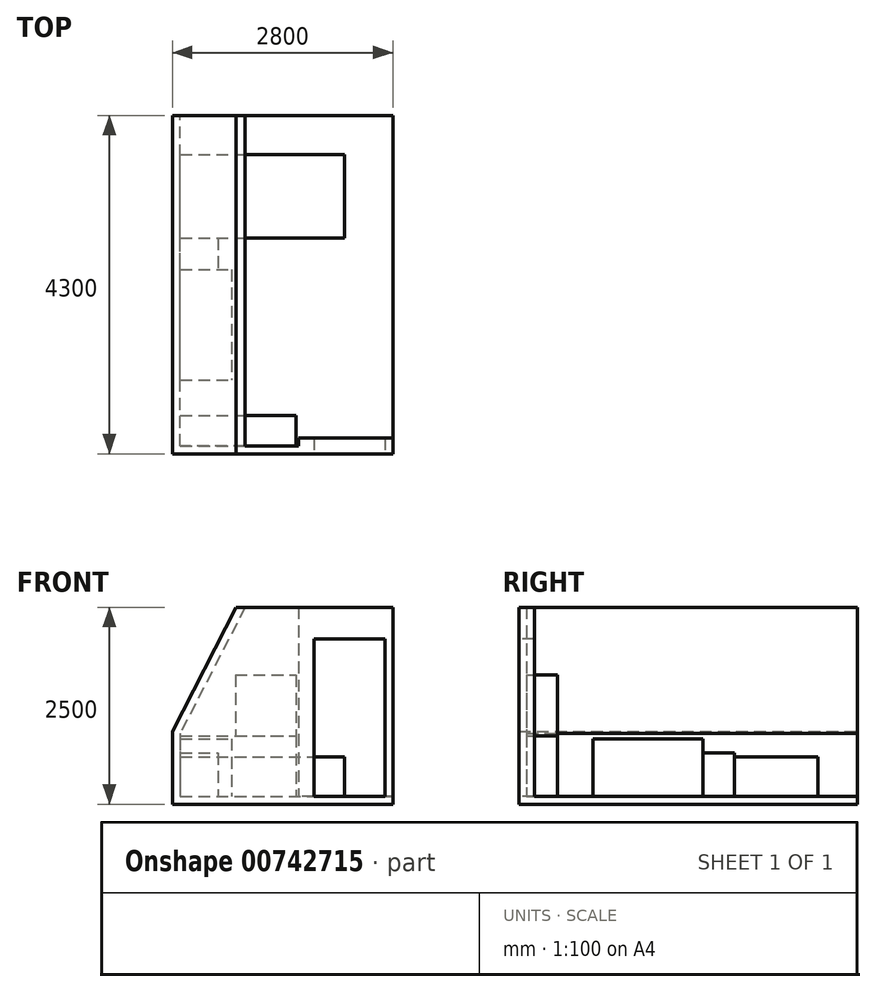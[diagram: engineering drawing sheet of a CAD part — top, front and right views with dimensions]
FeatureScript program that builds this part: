
annotation { "Feature Type Name" : "Feature", "Feature Type Description" : "" }
export const myFeature = defineFeature(function(context is Context, id is Id, definition is map)
    precondition{}
    {
        {
            var Q0;
            Q0=qCreatedBy(makeId("Front.planeOp"),FACE);
            var sketch = newSketch(context, id + "F0", { "sketchPlane" : qUnion([Q0])});
            skLineSegment(sketch, "E0", {"start": v(-1350, 800) * mm, "end": v(-1350, 0) * mm});
            skLineSegment(sketch, "E1", {"start": v(-1350, 0) * mm, "end": v(1350, 0) * mm});
            skLineSegment(sketch, "E2", {"start": v(1350, 0) * mm, "end": v(1350, 2400) * mm});
            skLineSegment(sketch, "E3", {"start": v(1350, 2400) * mm, "end": v(-525.38, 2400) * mm});
            skLineSegment(sketch, "E4", {"start": v(-525.38, 2400) * mm, "end": v(-1350, 800) * mm});
            skSolve(sketch);
        }
        {
            var Q0;
            Q0=makeQuery(id+"F0.imprint","IMPRINT",FACE,{"disambiguationData":[TD([[makeQuery(id+"F0.imprint","IMPRINT",EDGE,{"derivedFrom":sQuery(id+"F0.wireOp",EDGE,"E0")}),1.0]])]});
            extrude(context, id + "F1", {"entities" : qUnion([Q0]), "endBound" : BoundingType.SYMMETRIC, "depth" : 4200 * mm, "offsetDistance" : 25 * mm});
        }
        {
            var Q0;
            Q0=makeQuery(id+"F1.opExtrude","CAP_FACE",FACE,{"disambiguationData":[OSD([sQuery(id+"F0.wireOp",EDGE,"E0"),sQuery(id+"F0.wireOp",EDGE,"E1"),sQuery(id+"F0.wireOp",EDGE,"E2"),sQuery(id+"F0.wireOp",EDGE,"E3"),sQuery(id+"F0.wireOp",EDGE,"E4")])],"isStart":true});
            var Q1;
            Q1=makeQuery(id+"F1.opExtrude","SWEPT_FACE",FACE,{"disambiguationData":[OSD([sQuery(id+"F0.wireOp",EDGE,"E3")])]});
            var Q2;
            Q2=makeQuery(id+"F1.opExtrude","SWEPT_FACE",FACE,{"disambiguationData":[OSD([sQuery(id+"F0.wireOp",EDGE,"E2")])]});
            shell(context, id + "F2", {"entities" : qUnion([Q0, Q1, Q2]), "thickness" : 100 * mm, "oppositeDirection" : true});
        }
        {
            var Q0;
            Q0=makeQuery(id+"F2.opShell","OFFSET_FACE",FACE,{"disambiguationData":[OSD([sQuery(id+"F0.wireOp",EDGE,"E1")])]});
            var sketch = newSketch(context, id + "F3", { "sketchPlane" : qUnion([Q0])});
            skLineSegment(sketch, "E5.bottom", {"start": v(-1350, 1600) * mm, "end": v(740, 1600) * mm});
            skLineSegment(sketch, "E5.top", {"start": v(-1350, 540) * mm, "end": v(740, 540) * mm});
            skLineSegment(sketch, "E5.left", {"start": v(-1350, 1600) * mm, "end": v(-1350, 540) * mm});
            skLineSegment(sketch, "E5.right", {"start": v(740, 1600) * mm, "end": v(740, 540) * mm});
            skSolve(sketch);
        }
        {
            var Q0;
            Q0 = qSketchRegion(id + "F3", true);
            extrude(context, id + "F4", {"entities" : qUnion([Q0]), "depth" : 500 * mm, "offsetDistance" : 25 * mm});
        }
        {
            var Q0;
            Q0=makeQuery(id+"F2.opShell","OFFSET_FACE",FACE,{"disambiguationData":[OSD([sQuery(id+"F0.wireOp",EDGE,"E1")])]});
            var sketch = newSketch(context, id + "F5", { "sketchPlane" : qUnion([Q0])});
            skLineSegment(sketch, "E6.bottom", {"start": v(1350, -2100) * mm, "end": v(150, -2100) * mm});
            skLineSegment(sketch, "E6.top", {"start": v(1350, -2000) * mm, "end": v(150, -2000) * mm});
            skLineSegment(sketch, "E6.left", {"start": v(1350, -2100) * mm, "end": v(1350, -2000) * mm});
            skLineSegment(sketch, "E6.right", {"start": v(150, -2100) * mm, "end": v(150, -2000) * mm});
            skSolve(sketch);
        }
        {
            var Q0;
            Q0 = qSketchRegion(id + "F5", true);
            var Q1;
            Q1=makeQuery(id+"F1.opExtrude","SWEPT_FACE",FACE,{"disambiguationData":[OSD([sQuery(id+"F0.wireOp",EDGE,"E3")])]});
            extrude(context, id + "F6", {"entities" : qUnion([Q0]), "operationType" : NewBodyOperationType.ADD, "endBound" : BoundingType.UP_TO_SURFACE, "depth" : 25 * mm, "endBoundEntityFace" : qUnion([Q1]), "offsetDistance" : 25 * mm});
        }
        {
            var Q0;
            Q0=makeQuery(id+"F1.opExtrude","CAP_FACE",FACE,{"disambiguationData":[OSD([sQuery(id+"F0.wireOp",EDGE,"E0"),sQuery(id+"F0.wireOp",EDGE,"E1"),sQuery(id+"F0.wireOp",EDGE,"E2"),sQuery(id+"F0.wireOp",EDGE,"E3"),sQuery(id+"F0.wireOp",EDGE,"E4")])],"isStart":false});
            var sketch = newSketch(context, id + "F7", { "sketchPlane" : qUnion([Q0])});
            skLineSegment(sketch, "E7.bottom", {"start": v(1250, 0) * mm, "end": v(350, 0) * mm});
            skLineSegment(sketch, "E7.top", {"start": v(1250, 2000) * mm, "end": v(350, 2000) * mm});
            skLineSegment(sketch, "E7.left", {"start": v(1250, 0) * mm, "end": v(1250, 2000) * mm});
            skLineSegment(sketch, "E7.right", {"start": v(350, 0) * mm, "end": v(350, 2000) * mm});
            skSolve(sketch);
        }
        {
            var Q0;
            Q0 = qSketchRegion(id + "F7", true);
            extrude(context, id + "F8", {"entities" : qUnion([Q0]), "operationType" : NewBodyOperationType.REMOVE, "oppositeDirection" : true, "depth" : 1000 * mm, "offsetDistance" : 25 * mm});
        }
        {
            var Q0;
            Q0=makeQuery(id+"F8.boolean.opBoolean","MERGE",FACE,{"derivedFrom":[makeQuery(id+"F2.opShell","OFFSET_FACE",FACE,{"disambiguationData":[OSD([sQuery(id+"F0.wireOp",EDGE,"E1")])]}),makeQuery(id+"F8.opExtrude","SWEPT_FACE",FACE,{"disambiguationData":[OSD([sQuery(id+"F7.wireOp",EDGE,"E7.bottom")])]})]});
            var sketch = newSketch(context, id + "F9", { "sketchPlane" : qUnion([Q0])});
            skLineSegment(sketch, "E8.bottom", {"start": v(-1350, -2100) * mm, "end": v(120, -2100) * mm});
            skLineSegment(sketch, "E8.top", {"start": v(-1350, -1710) * mm, "end": v(120, -1710) * mm});
            skLineSegment(sketch, "E8.left", {"start": v(-1350, -2100) * mm, "end": v(-1350, -1710) * mm});
            skLineSegment(sketch, "E8.right", {"start": v(120, -2100) * mm, "end": v(120, -1710) * mm});
            skSolve(sketch);
        }
        {
            var Q0;
            Q0 = qSketchRegion(id + "F9", true);
            extrude(context, id + "F10", {"entities" : qUnion([Q0]), "depth" : 770 * mm, "offsetDistance" : 25 * mm});
        }
        {
            var Q0;
            Q0=makeQuery(id+"F10.opExtrude","CAP_FACE",FACE,{"disambiguationData":[OSD([sQuery(id+"F9.wireOp",EDGE,"E8.bottom"),sQuery(id+"F9.wireOp",EDGE,"E8.top"),sQuery(id+"F9.wireOp",EDGE,"E8.left"),sQuery(id+"F9.wireOp",EDGE,"E8.right")])],"isStart":false});
            var sketch = newSketch(context, id + "F11", { "sketchPlane" : qUnion([Q0])});
            skLineSegment(sketch, "E9.bottom", {"start": v(120, -2100) * mm, "end": v(-650, -2100) * mm});
            skLineSegment(sketch, "E9.top", {"start": v(120, -1710) * mm, "end": v(-650, -1710) * mm});
            skLineSegment(sketch, "E9.left", {"start": v(120, -2100) * mm, "end": v(120, -1710) * mm});
            skLineSegment(sketch, "E9.right", {"start": v(-650, -2100) * mm, "end": v(-650, -1710) * mm});
            skSolve(sketch);
        }
        {
            var Q0;
            Q0 = qSketchRegion(id + "F11", true);
            extrude(context, id + "F12", {"entities" : qUnion([Q0]), "depth" : 770 * mm, "offsetDistance" : 25 * mm});
        }
        {
            var Q0;
            Q0=makeQuery(id+"F8.boolean.opBoolean","MERGE",FACE,{"derivedFrom":[makeQuery(id+"F2.opShell","OFFSET_FACE",FACE,{"disambiguationData":[OSD([sQuery(id+"F0.wireOp",EDGE,"E1")])]}),makeQuery(id+"F8.opExtrude","SWEPT_FACE",FACE,{"disambiguationData":[OSD([sQuery(id+"F7.wireOp",EDGE,"E7.bottom")])]})]});
            var sketch = newSketch(context, id + "F13", { "sketchPlane" : qUnion([Q0])});
            skLineSegment(sketch, "E10.bottom", {"start": v(-1350, 540) * mm, "end": v(-870, 540) * mm});
            skLineSegment(sketch, "E10.top", {"start": v(-1350, 140) * mm, "end": v(-870, 140) * mm});
            skLineSegment(sketch, "E10.left", {"start": v(-1350, 540) * mm, "end": v(-1350, 140) * mm});
            skLineSegment(sketch, "E10.right", {"start": v(-870, 540) * mm, "end": v(-870, 140) * mm});
            skSolve(sketch);
        }
        {
            var Q0;
            Q0 = qSketchRegion(id + "F13", true);
            extrude(context, id + "F14", {"entities" : qUnion([Q0]), "depth" : 550 * mm, "offsetDistance" : 25 * mm});
        }
        {
            var Q0;
            Q0=makeQuery(id+"F8.boolean.opBoolean","MERGE",FACE,{"derivedFrom":[makeQuery(id+"F2.opShell","OFFSET_FACE",FACE,{"disambiguationData":[OSD([sQuery(id+"F0.wireOp",EDGE,"E1")])]}),makeQuery(id+"F8.opExtrude","SWEPT_FACE",FACE,{"disambiguationData":[OSD([sQuery(id+"F7.wireOp",EDGE,"E7.bottom")])]})]});
            var sketch = newSketch(context, id + "F15", { "sketchPlane" : qUnion([Q0])});
            skLineSegment(sketch, "E11.bottom", {"start": v(-1350, 140) * mm, "end": v(-700, 140) * mm});
            skLineSegment(sketch, "E11.top", {"start": v(-1350, -1260) * mm, "end": v(-700, -1260) * mm});
            skLineSegment(sketch, "E11.left", {"start": v(-1350, 140) * mm, "end": v(-1350, -1260) * mm});
            skLineSegment(sketch, "E11.right", {"start": v(-700, 140) * mm, "end": v(-700, -1260) * mm});
            skSolve(sketch);
        }
        {
            var Q0;
            Q0 = qSketchRegion(id + "F15", true);
            extrude(context, id + "F16", {"entities" : qUnion([Q0]), "depth" : 730 * mm, "offsetDistance" : 25 * mm});
        }
    });
